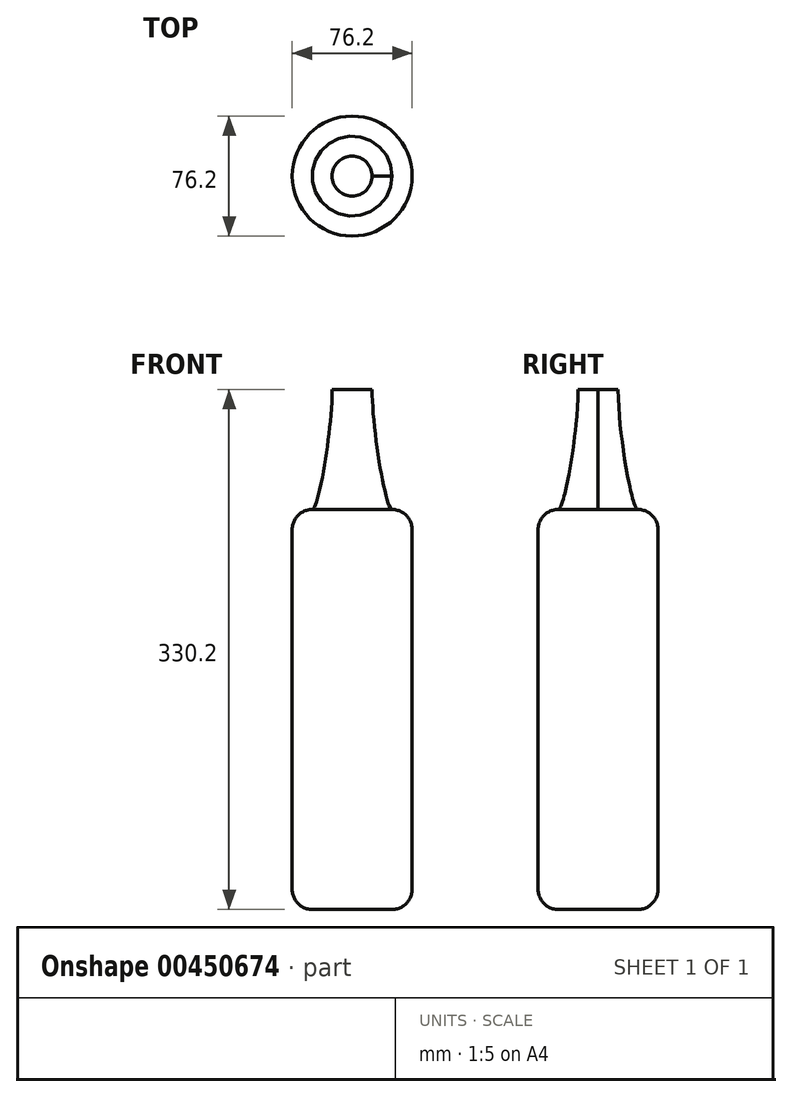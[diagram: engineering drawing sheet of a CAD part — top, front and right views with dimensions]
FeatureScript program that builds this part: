
annotation { "Feature Type Name" : "Feature", "Feature Type Description" : "" }
export const myFeature = defineFeature(function(context is Context, id is Id, definition is map)
    precondition{}
    {
        {
            var Q0;
            Q0=qCreatedBy(makeId("Top.planeOp"),FACE);
            var sketch = newSketch(context, id + "F0", { "sketchPlane" : qUnion([Q0])});
            skCircle(sketch, "E0", {"center": v(0, 0) * mm, "radius": 38.1 * mm});
            skSolve(sketch);
        }
        {
            var Q0;
            Q0=makeQuery(id+"F0.imprint","IMPRINT",FACE,{"disambiguationData":[TD([[makeQuery(id+"F0.imprint","IMPRINT",EDGE,{"derivedFrom":sQuery(id+"F0.wireOp",EDGE,"E0")}),1.0]])]});
            extrude(context, id + "F1", {"entities" : qUnion([Q0]), "depth" : 254 * mm});
        }
        {
            var Q0;
            Q0=makeQuery(id+"F1.opExtrude","CAP_EDGE",EDGE,{"disambiguationData":[OSD([sQuery(id+"F0.wireOp",EDGE,"E0")])],"isStart":true});
            fillet(context, id + "F2", {"entities" : qUnion([Q0]), "radius" : 12.7 * mm, "tangentPropagation" : true, "allowEdgeOverflow" : false});
        }
        {
            var Q0;
            Q0=makeQuery(id+"F1.opExtrude","CAP_EDGE",EDGE,{"disambiguationData":[OSD([sQuery(id+"F0.wireOp",EDGE,"E0")])],"isStart":false});
            fillet(context, id + "F3", {"entities" : qUnion([Q0]), "radius" : 12.7 * mm, "tangentPropagation" : true, "allowEdgeOverflow" : false});
        }
        {
            var Q0;
            Q0=qCreatedBy(makeId("Top.planeOp"),FACE);
            cPlane(context, id + "F4", {"entities" : qUnion([Q0]), "cplaneType" : CPlaneType.OFFSET, "offset" : 330.2 * mm, "width" : 152.4 * mm, "height" : 152.4 * mm});
        }
        {
            var Q0;
            Q0=qCreatedBy(id+"F4.planeOp",FACE);
            var sketch = newSketch(context, id + "F5", { "sketchPlane" : qUnion([Q0])});
            skCircle(sketch, "E1", {"center": v(0, 0) * mm, "radius": 12.7 * mm});
            skSolve(sketch);
        }
        {
            var Q0;
            Q0=makeQuery(id+"F1.opExtrude","CAP_FACE",FACE,{"disambiguationData":[OSD([sQuery(id+"F0.wireOp",EDGE,"E0")])],"isStart":false});
            var sketch = newSketch(context, id + "F6", { "sketchPlane" : qUnion([Q0])});
            skCircle(sketch, "E2.0", {"center": v(0, 0) * mm, "radius": 25.4 * mm});
            skSolve(sketch);
        }
        {
            var Q0;
            Q0=makeQuery(id+"F5.imprint","IMPRINT",FACE,{"disambiguationData":[TD([[makeQuery(id+"F5.imprint","IMPRINT",EDGE,{"derivedFrom":sQuery(id+"F5.wireOp",EDGE,"E1")}),1.0]])]});
            var Q1;
            Q1=makeQuery(id+"F6.imprint","IMPRINT",FACE,{"disambiguationData":[TD([[makeQuery(id+"F6.imprint","IMPRINT",EDGE,{"derivedFrom":sQuery(id+"F6.wireOp",EDGE,"E2.0")}),1.0]])]});
            loft(context, id + "F7", {"operationType" : NewBodyOperationType.ADD, "startCondition" : LoftEndDerivativeType.NORMAL_TO_PROFILE, "startMagnitude" : 1, "endCondition" : LoftEndDerivativeType.TANGENT_TO_PROFILE, "endMagnitude" : 1, "sheetProfilesArray" : [{ "sheetProfileEntities" : qUnion([Q0]) }, { "sheetProfileEntities" : qUnion([Q1]) }]});
        }
    });
